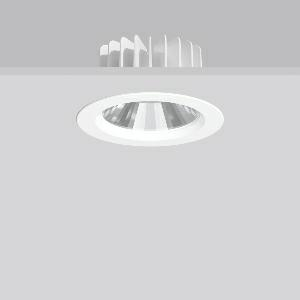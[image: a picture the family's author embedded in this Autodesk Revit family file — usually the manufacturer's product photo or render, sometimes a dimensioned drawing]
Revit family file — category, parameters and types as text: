
# Revit family: ledona_round_ip65_901797_002_76_ecb0
name_source: partatom
category: Lighting Fixtures
units: mm (PartAtom-declared; Revit-internal decimal feet)

## family parameters
Cut with Voids When Loaded = No
Host = Face
Light Source = No
Part Type = Normal
Room Calculation Point = No
Round Connector Dimension = Use Diameter
Shared = No

## types (1)
- MultiLumen 1 (1 x LED Modul 930, 1600 lm, 3000)
    Apparent Load = 12 VA
    Approval mark = CE
    CIE Flux Codes = 89 99 100 100 100
    Color Rendering = 90
    Color Temperature = 3000
    Default Elevation = 1800 mm
    Height = 0 mm  [stored 0 ft]
    Lamp = 1 x LED Modul 930
    Lamp Light Flux = 1600 lm
    Lamp count = 1
    Length = 180 mm
    Lifetime = 50000 h
    Luminous efficacy = 133 lm/W
    Manufacturer = RZB
    ModVariant = No
    Model = 901797.002.76
    Mounting Place = Ceiling
    Mounting Type = Recessed
    Number of Poles = 1
    OnlyDefault = Yes
    Power Factor = 1
    Product Name = LEDONA round IP65
    Product group = Recessed downlights
    ProductGroupID = 402
    Protection Class = Protection class II
    Protection Degree = IP 65
    RLX_Detail_Level = 1
    RLX_Emergency_Light_Flux = 0 lm
    RLX_Emergency_Type = 0
    RLX_Emergency_Type_DB = No
    RlxData = <blob elided: 38673 chars, md5=94b7d8d8>
    Socket = socket
    Standby Power = 0 W
    System Light Flux = 1600 lm
    System Power = 12 W
    Type Comments = MultiLumen 1
    Type Image = 901346.002.jpg
    URL = http://relux.com
    VarID = multilumen_1
    Voltage = 230 V
    Voltage Range = 220-240 V
    Weight = 0.00 kg
    Width = 0 mm  [stored 0 ft]

note: [stored X ft] marks values corroborated as IEEE doubles in the binary element streams (Revit-internal decimal feet)

## geometry (parser evidence)
native form markers: Blend x4, Sweep x8
no freeform markers — native parametric forms only
